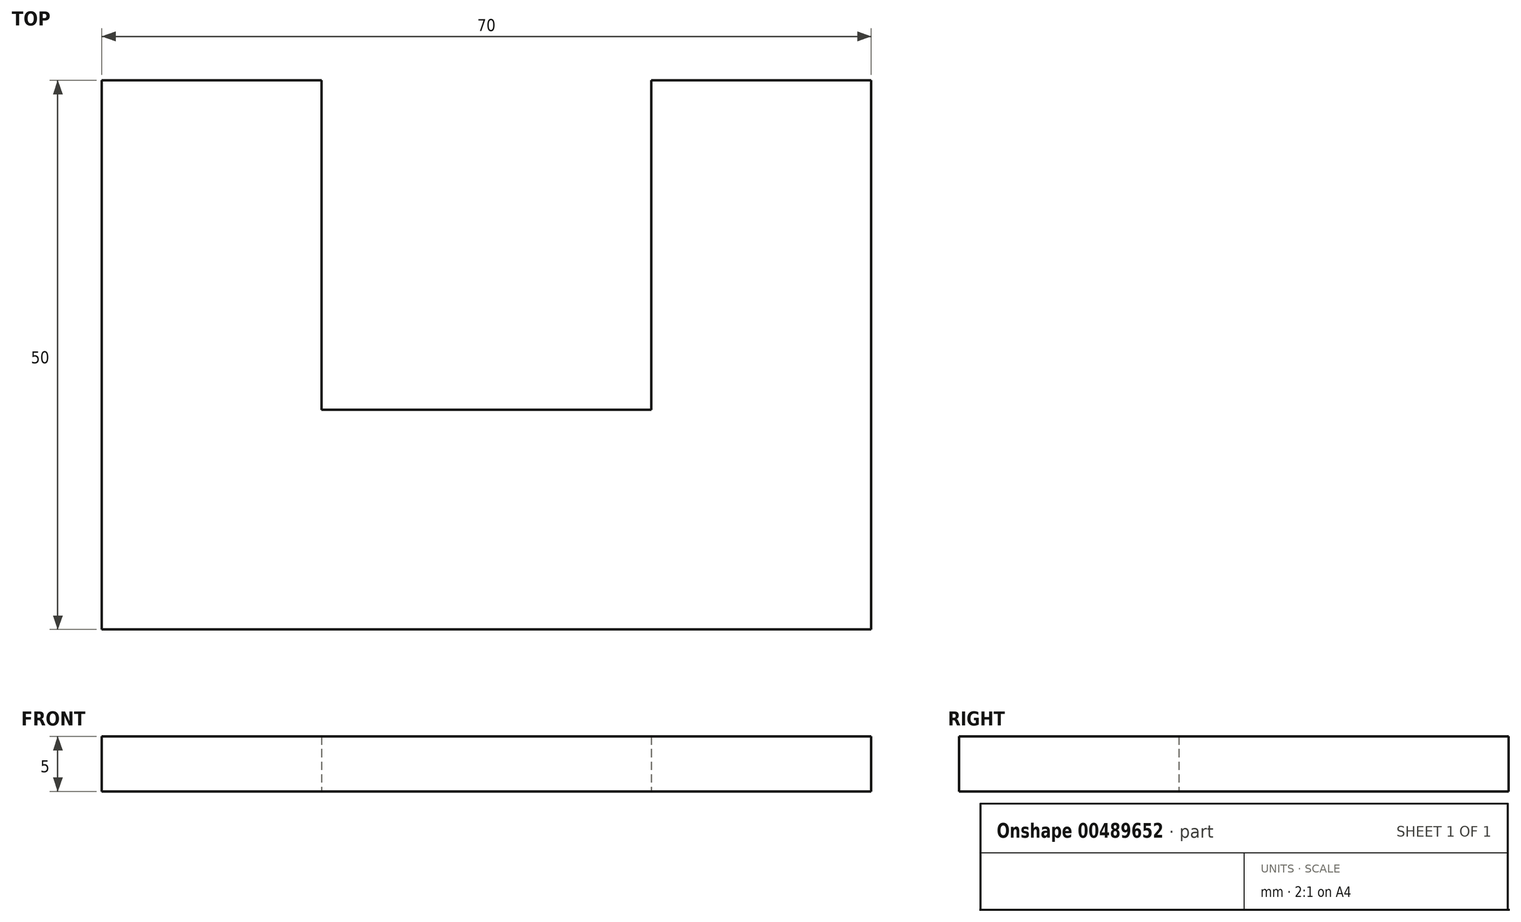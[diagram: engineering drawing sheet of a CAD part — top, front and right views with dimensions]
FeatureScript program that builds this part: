
annotation { "Feature Type Name" : "Feature", "Feature Type Description" : "" }
export const myFeature = defineFeature(function(context is Context, id is Id, definition is map)
    precondition{}
    {
        {
            var Q0;
            Q0=qCreatedBy(makeId("Top.planeOp"),FACE);
            var sketch = newSketch(context, id + "F0", { "sketchPlane" : qUnion([Q0])});
            skLineSegment(sketch, "E0", {"start": v(0, 0) * mm, "end": v(70, 0) * mm});
            skLineSegment(sketch, "E1", {"start": v(70, 0) * mm, "end": v(70, 50) * mm});
            skLineSegment(sketch, "E2", {"start": v(50, 50) * mm, "end": v(50, 20) * mm});
            skLineSegment(sketch, "E3", {"start": v(50, 20) * mm, "end": v(20, 20) * mm});
            skLineSegment(sketch, "E4", {"start": v(20, 20) * mm, "end": v(20, 50) * mm});
            skLineSegment(sketch, "E5", {"start": v(20, 50) * mm, "end": v(0, 50) * mm});
            skLineSegment(sketch, "E6", {"start": v(0, 50) * mm, "end": v(0, 0) * mm});
            skLineSegment(sketch, "E7", {"start": v(50, 50) * mm, "end": v(70, 50) * mm});
            skLineSegment(sketch, "E8", {"start": v(20, 20) * mm, "end": v(20, 0) * mm, "construction": true});
            skSolve(sketch);
        }
        {
            var Q0;
            Q0=makeQuery(id+"F0.imprint","IMPRINT",FACE,{"disambiguationData":[TD([[makeQuery(id+"F0.imprint","IMPRINT",EDGE,{"derivedFrom":sQuery(id+"F0.wireOp",EDGE,"E0")}),1.0]])]});
            extrude(context, id + "F1", {"entities" : qUnion([Q0]), "depth" : 5 * mm});
        }
    });
